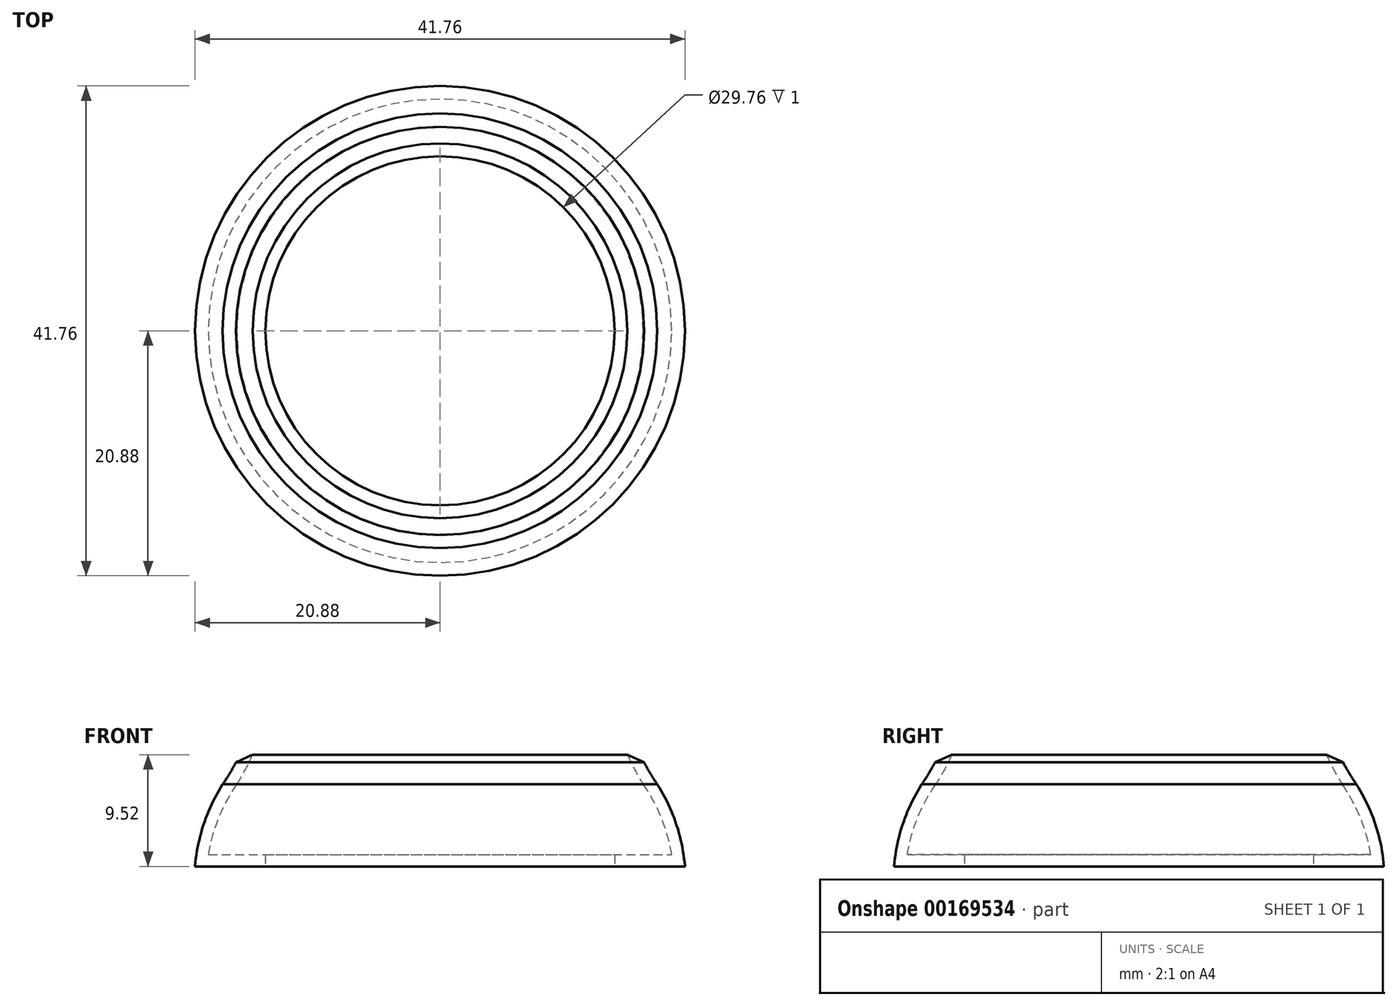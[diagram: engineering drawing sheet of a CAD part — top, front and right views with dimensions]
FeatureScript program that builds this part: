
annotation { "Feature Type Name" : "Feature", "Feature Type Description" : "" }
export const myFeature = defineFeature(function(context is Context, id is Id, definition is map)
    precondition{}
    {
        {
            var Q0;
            Q0=qCreatedBy(makeId("Top.planeOp"),FACE);
            var sketch = newSketch(context, id + "F0", { "sketchPlane" : qUnion([Q0])});
            skCircle(sketch, "E0", {"center": v(0, 0) * mm, "radius": 19.75 * mm});
            skSolve(sketch);
        }
        {
            var Q0;
            Q0=qCreatedBy(makeId("Front.planeOp"),FACE);
            var sketch = newSketch(context, id + "F1", { "sketchPlane" : qUnion([Q0])});
            skArc(sketch, "E1", {"start": v(-17.32, 6) * mm, "mid": v(-18.88, 3.14) * mm, "end": v(-19.75, 0) * mm});
            skLineSegment(sketch, "E2", {"start": v(-19.75, 0) * mm, "end": v(-14.88, 0) * mm});
            skLineSegment(sketch, "E3", {"start": v(-14.88, 0) * mm, "end": v(-14.88, -1) * mm});
            skLineSegment(sketch, "E4", {"start": v(-14.88, -1) * mm, "end": v(-20.88, -1) * mm});
            skArc(sketch, "E5.0", {"start": v(-18.53, 6) * mm, "mid": v(-20.13, 2.64) * mm, "end": v(-20.88, -1) * mm});
            skArc(sketch, "E6", {"start": v(-18.53, 6) * mm, "mid": v(-17.93, 6.92) * mm, "end": v(-17.4, 7.87) * mm});
            skArc(sketch, "E7.0", {"start": v(-17.32, 6) * mm, "mid": v(-16.6, 7.23) * mm, "end": v(-15.97, 8.52) * mm});
            skLineSegment(sketch, "E8", {"start": v(-17.4, 7.87) * mm, "end": v(-15.97, 8.52) * mm});
            skSolve(sketch);
        }
        {
            var Q0;
            Q0=makeQuery(id+"F1.imprint","IMPRINT",FACE,{"disambiguationData":[TD([[makeQuery(id+"F1.imprint","IMPRINT",EDGE,{"derivedFrom":sQuery(id+"F1.wireOp",EDGE,"E1")}),-1.0]])]});
            var Q1;
            Q1=sQuery(id+"F0.wireOp",EDGE,"E0");
            revolve(context, id + "F2", {"entities" : qUnion([Q0]), "axis" : qUnion([Q1]), "revolveType" : RevolveType.FULL});
        }
    });
